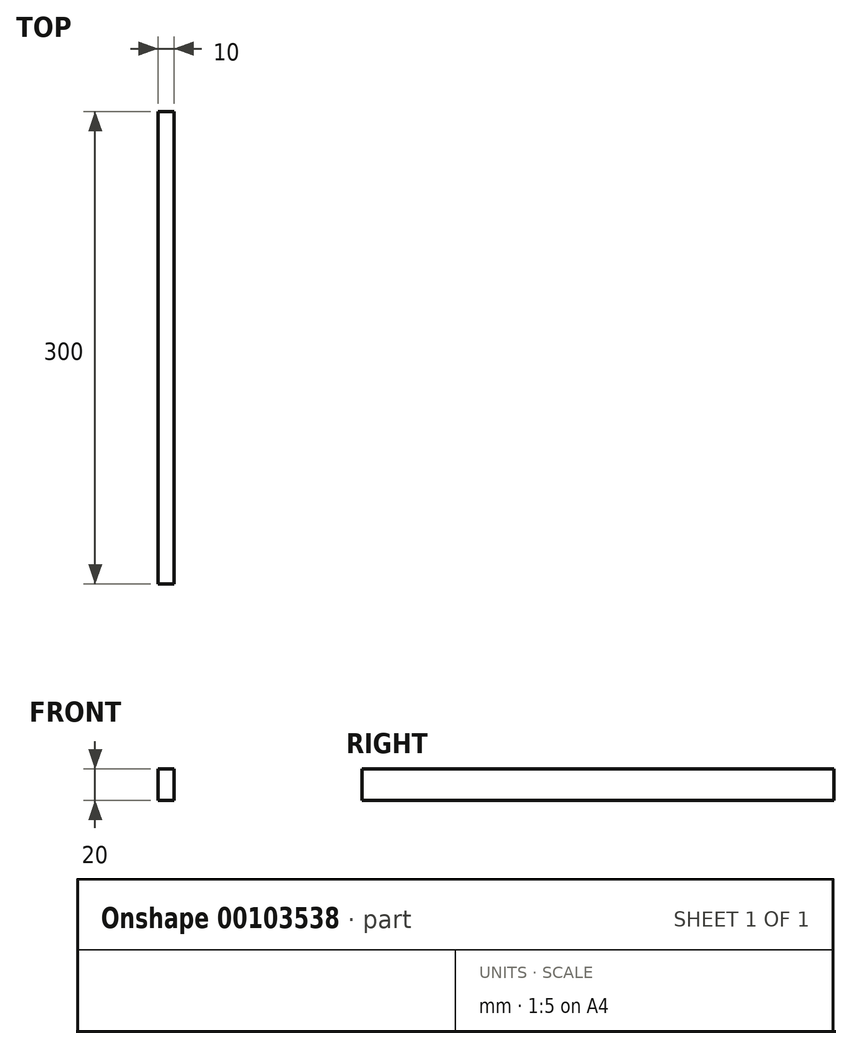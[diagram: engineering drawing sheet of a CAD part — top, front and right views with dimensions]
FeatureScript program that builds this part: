
annotation { "Feature Type Name" : "Feature", "Feature Type Description" : "" }
export const myFeature = defineFeature(function(context is Context, id is Id, definition is map)
    precondition{}
    {
        {
            var Q0;
            Q0=qCreatedBy(makeId("Front.planeOp"),FACE);
            var sketch = newSketch(context, id + "F0", { "sketchPlane" : qUnion([Q0])});
            skLineSegment(sketch, "E0.bottom", {"start": v(5, -10) * mm, "end": v(-5, -10) * mm});
            skLineSegment(sketch, "E0.top", {"start": v(5, 10) * mm, "end": v(-5, 10) * mm});
            skLineSegment(sketch, "E0.left", {"start": v(5, -10) * mm, "end": v(5, 10) * mm});
            skLineSegment(sketch, "E0.right", {"start": v(-5, -10) * mm, "end": v(-5, 10) * mm});
            skPoint(sketch, "E0.middle", {"position": v(0, 0) * mm});
            skSolve(sketch);
        }
        {
            var Q0;
            Q0=makeQuery(id+"F0.imprint","IMPRINT",FACE,{"disambiguationData":[TD([[makeQuery(id+"F0.imprint","IMPRINT",EDGE,{"derivedFrom":sQuery(id+"F0.wireOp",EDGE,"E0.bottom")}),-1.0]])]});
            extrude(context, id + "F1", {"entities" : qUnion([Q0]), "depth" : 300 * mm});
        }
    });
